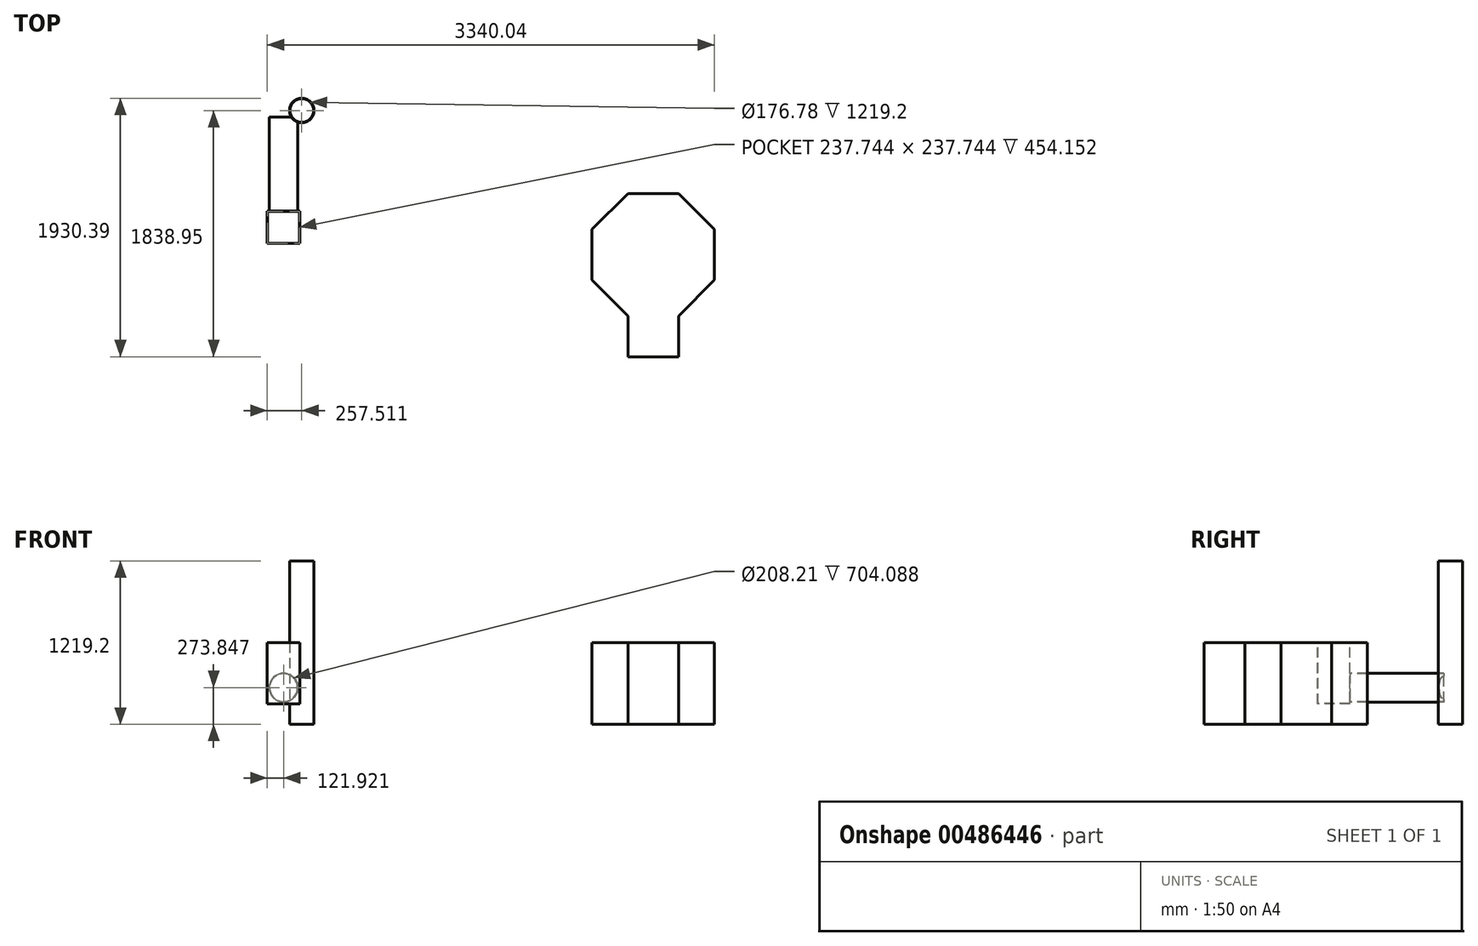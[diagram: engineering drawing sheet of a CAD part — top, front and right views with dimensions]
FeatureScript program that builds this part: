
annotation { "Feature Type Name" : "Feature", "Feature Type Description" : "" }
export const myFeature = defineFeature(function(context is Context, id is Id, definition is map)
    precondition{}
    {
        {
            var Q0;
            Q0=qCreatedBy(makeId("Top.planeOp"),FACE);
            var sketch = newSketch(context, id + "F0", { "sketchPlane" : qUnion([Q0])});
            skCircle(sketch, "E0.cCircle", {"center": v(0, 0) * mm, "radius": 457.2 * mm, "construction": true});
            skLineSegment(sketch, "E0.0", {"start": v(189.38, -457.2) * mm, "end": v(-189.38, -457.2) * mm});
            skLineSegment(sketch, "E0.1", {"start": v(-189.38, -457.2) * mm, "end": v(-457.2, -189.38) * mm});
            skLineSegment(sketch, "E0.2", {"start": v(-457.2, -189.38) * mm, "end": v(-457.2, 189.38) * mm});
            skLineSegment(sketch, "E0.3", {"start": v(-457.2, 189.38) * mm, "end": v(-189.38, 457.2) * mm});
            skLineSegment(sketch, "E0.4", {"start": v(-189.38, 457.2) * mm, "end": v(189.38, 457.2) * mm});
            skLineSegment(sketch, "E0.5", {"start": v(189.38, 457.2) * mm, "end": v(457.2, 189.38) * mm});
            skLineSegment(sketch, "E0.6", {"start": v(457.2, 189.38) * mm, "end": v(457.2, -189.38) * mm});
            skLineSegment(sketch, "E0.7", {"start": v(457.2, -189.38) * mm, "end": v(189.38, -457.2) * mm});
            skPoint(sketch, "E0.0.midPoint", {"position": v(0, -457.2) * mm});
            skSolve(sketch);
        }
        {
            var Q0;
            Q0 = qSketchRegion(id + "F0", true);
            extrude(context, id + "F1", {"entities" : qUnion([Q0]), "depth" : 609.6 * mm});
        }
        {
            var Q0;
            Q0=makeQuery(id+"F1.opExtrude","SWEPT_FACE",FACE,{"disambiguationData":[OSD([sQuery(id+"F0.wireOp",EDGE,"E0.0")])]});
            extrude(context, id + "F2", {"entities" : qUnion([Q0]), "operationType" : NewBodyOperationType.ADD, "depth" : 304.8 * mm});
        }
        {
            var Q0;
            {var subQ0=sQuery(id+"F0.wireOp",EDGE,"E0.0");Q0=makeQuery(id+"F2.boolean.opBoolean","MERGE",FACE,{"derivedFrom":[makeQuery(id+"F1.opExtrude","CAP_FACE",FACE,{"disambiguationData":[OSD([subQ0,sQuery(id+"F0.wireOp",EDGE,"E0.1"),sQuery(id+"F0.wireOp",EDGE,"E0.2"),sQuery(id+"F0.wireOp",EDGE,"E0.3"),sQuery(id+"F0.wireOp",EDGE,"E0.4"),sQuery(id+"F0.wireOp",EDGE,"E0.5"),sQuery(id+"F0.wireOp",EDGE,"E0.6"),sQuery(id+"F0.wireOp",EDGE,"E0.7")])],"isStart":false}),makeQuery(id+"F2.opExtrude","SWEPT_FACE",FACE,{"disambiguationData":[OSD([subQ0]),TDD([makeQuery(id+"F1.opExtrude","CAP_EDGE",EDGE,{"disambiguationData":[OSD([subQ0])],"isStart":false})])]})]});}
            var sketch = newSketch(context, id + "F3", { "sketchPlane" : qUnion([Q0])});
            skLineSegment(sketch, "E1.bottom", {"start": v(-2882.84, 327.32) * mm, "end": v(-2639, 327.32) * mm});
            skLineSegment(sketch, "E1.top", {"start": v(-2882.84, 83.48) * mm, "end": v(-2639, 83.48) * mm});
            skLineSegment(sketch, "E1.left", {"start": v(-2882.84, 327.32) * mm, "end": v(-2882.84, 83.48) * mm});
            skLineSegment(sketch, "E1.right", {"start": v(-2639, 327.32) * mm, "end": v(-2639, 83.48) * mm});
            skSolve(sketch);
        }
        {
            var Q0;
            Q0=makeQuery(id+"F3.imprint","IMPRINT",FACE,{"disambiguationData":[TD([[makeQuery(id+"F3.imprint","IMPRINT",EDGE,{"derivedFrom":sQuery(id+"F3.wireOp",EDGE,"E1.bottom")}),-1.0]])]});
            extrude(context, id + "F4", {"entities" : qUnion([Q0]), "oppositeDirection" : true, "depth" : 457.2 * mm});
        }
        {
            var Q0;
            Q0=makeQuery(id+"F4.opExtrude","SWEPT_FACE",FACE,{"disambiguationData":[OSD([sQuery(id+"F3.wireOp",EDGE,"E1.bottom")])]});
            var sketch = newSketch(context, id + "F5", { "sketchPlane" : qUnion([Q0])});
            skCircle(sketch, "E2", {"center": v(2760.92, 273.85) * mm, "radius": 107.15 * mm});
            skPoint(sketch, "E2.centerSnap0", {"position": v(2760.92, 152.4) * mm});
            skPoint(sketch, "E2.perimeterSnap0", {"position": v(2639, 381) * mm});
            skPoint(sketch, "E2.perimeterSnap1", {"position": v(2760.92, 152.4) * mm});
            skSolve(sketch);
        }
        {
            var Q0;
            Q0=makeQuery(id+"F5.imprint","IMPRINT",FACE,{"disambiguationData":[TD([[makeQuery(id+"F5.imprint","IMPRINT",EDGE,{"derivedFrom":sQuery(id+"F5.wireOp",EDGE,"E2")}),1.0]])]});
            extrude(context, id + "F6", {"entities" : qUnion([Q0]), "operationType" : NewBodyOperationType.ADD, "depth" : 701.04 * mm});
        }
        {
            var Q0;
            Q0=makeQuery(id+"F4.opExtrude","CAP_FACE",FACE,{"disambiguationData":[OSD([sQuery(id+"F3.wireOp",EDGE,"E1.bottom"),sQuery(id+"F3.wireOp",EDGE,"E1.top"),sQuery(id+"F3.wireOp",EDGE,"E1.left"),sQuery(id+"F3.wireOp",EDGE,"E1.right")])],"isStart":true});
            var Q1;
            Q1=makeQuery(id+"F6.opExtrude","CAP_FACE",FACE,{"disambiguationData":[OSD([sQuery(id+"F5.wireOp",EDGE,"E2")])],"isStart":false});
            shell(context, id + "F7", {"entities" : qUnion([Q0, Q1]), "thickness" : 3.05 * mm});
        }
        {
            var Q0;
            Q0=qCreatedBy(makeId("Top.planeOp"),FACE);
            var sketch = newSketch(context, id + "F8", { "sketchPlane" : qUnion([Q0])});
            skCircle(sketch, "E3", {"center": v(-2625.33, 1076.95) * mm, "radius": 91.44 * mm});
            skSolve(sketch);
        }
        {
            var Q0;
            Q0 = qSketchRegion(id + "F8", true);
            extrude(context, id + "F9", {"entities" : qUnion([Q0]), "operationType" : NewBodyOperationType.ADD, "depth" : 1219.2 * mm});
        }
        {
            var Q0;
            Q0=makeQuery(id+"F9.opExtrude","CAP_FACE",FACE,{"disambiguationData":[OSD([sQuery(id+"F8.wireOp",EDGE,"E3")])],"isStart":false});
            var Q1;
            Q1=makeQuery(id+"F9.opExtrude","CAP_FACE",FACE,{"disambiguationData":[OSD([sQuery(id+"F8.wireOp",EDGE,"E3")])],"isStart":true});
            shell(context, id + "F10", {"entities" : qUnion([Q0, Q1]), "thickness" : 3.05 * mm});
        }
    });
